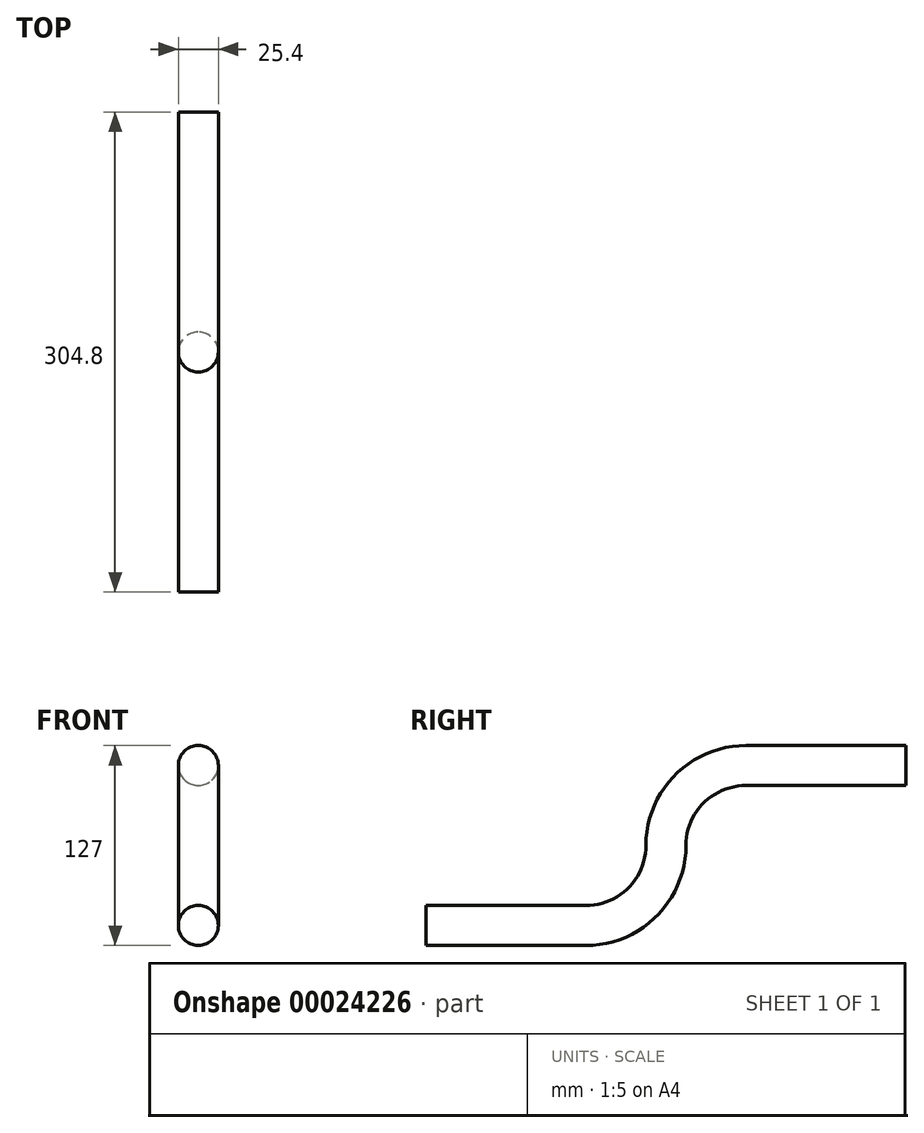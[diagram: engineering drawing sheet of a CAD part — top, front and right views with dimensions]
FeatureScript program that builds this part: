
annotation { "Feature Type Name" : "Feature", "Feature Type Description" : "" }
export const myFeature = defineFeature(function(context is Context, id is Id, definition is map)
    precondition{}
    {
        {
            var Q0;
            Q0=qCreatedBy(makeId("Front.planeOp"),FACE);
            var sketch = newSketch(context, id + "F0", { "sketchPlane" : qUnion([Q0])});
            skCircle(sketch, "E0", {"center": v(0, 0) * mm, "radius": 12.7 * mm});
            skSolve(sketch);
        }
        {
            var Q0;
            Q0=qCreatedBy(makeId("Right.planeOp"),FACE);
            var sketch = newSketch(context, id + "F1", { "sketchPlane" : qUnion([Q0])});
            skLineSegment(sketch, "E1", {"start": v(0, 0) * mm, "end": v(101.6, 0) * mm});
            skLineSegment(sketch, "E2", {"start": v(152.4, 50.8) * mm, "end": v(152.4, 50.8) * mm});
            skLineSegment(sketch, "E3", {"start": v(203.2, 101.6) * mm, "end": v(304.8, 101.6) * mm});
            skPoint(sketch, "E4.visualSharp", {"position": v(152.4, 0) * mm});
            skArc(sketch, "E4.filletArc", {"start": v(101.6, 0) * mm, "mid": v(137.52, 14.88) * mm, "end": v(152.4, 50.8) * mm});
            skPoint(sketch, "E5.visualSharp", {"position": v(152.4, 101.6) * mm});
            skArc(sketch, "E5.filletArc", {"start": v(203.2, 101.6) * mm, "mid": v(167.28, 86.72) * mm, "end": v(152.4, 50.8) * mm});
            skSolve(sketch);
        }
        {
            var Q0;
            Q0=makeQuery(id+"F0.imprint","IMPRINT",FACE,{"disambiguationData":[TD([[makeQuery(id+"F0.imprint","IMPRINT",EDGE,{"derivedFrom":sQuery(id+"F0.wireOp",EDGE,"E0")}),1.0]])]});
            var Q1;
            Q1=sQuery(id+"F1.wireOp",EDGE,"E4.filletArc");
            var Q2;
            Q2=sQuery(id+"F1.wireOp",EDGE,"E1");
            var Q3;
            Q3=sQuery(id+"F1.wireOp",EDGE,"E5.filletArc");
            var Q4;
            Q4=sQuery(id+"F1.wireOp",EDGE,"E3");
            sweep(context, id + "F2", {"profiles" : qUnion([Q0]), "path" : qUnion([Q1, Q2, Q3, Q4])});
        }
    });
